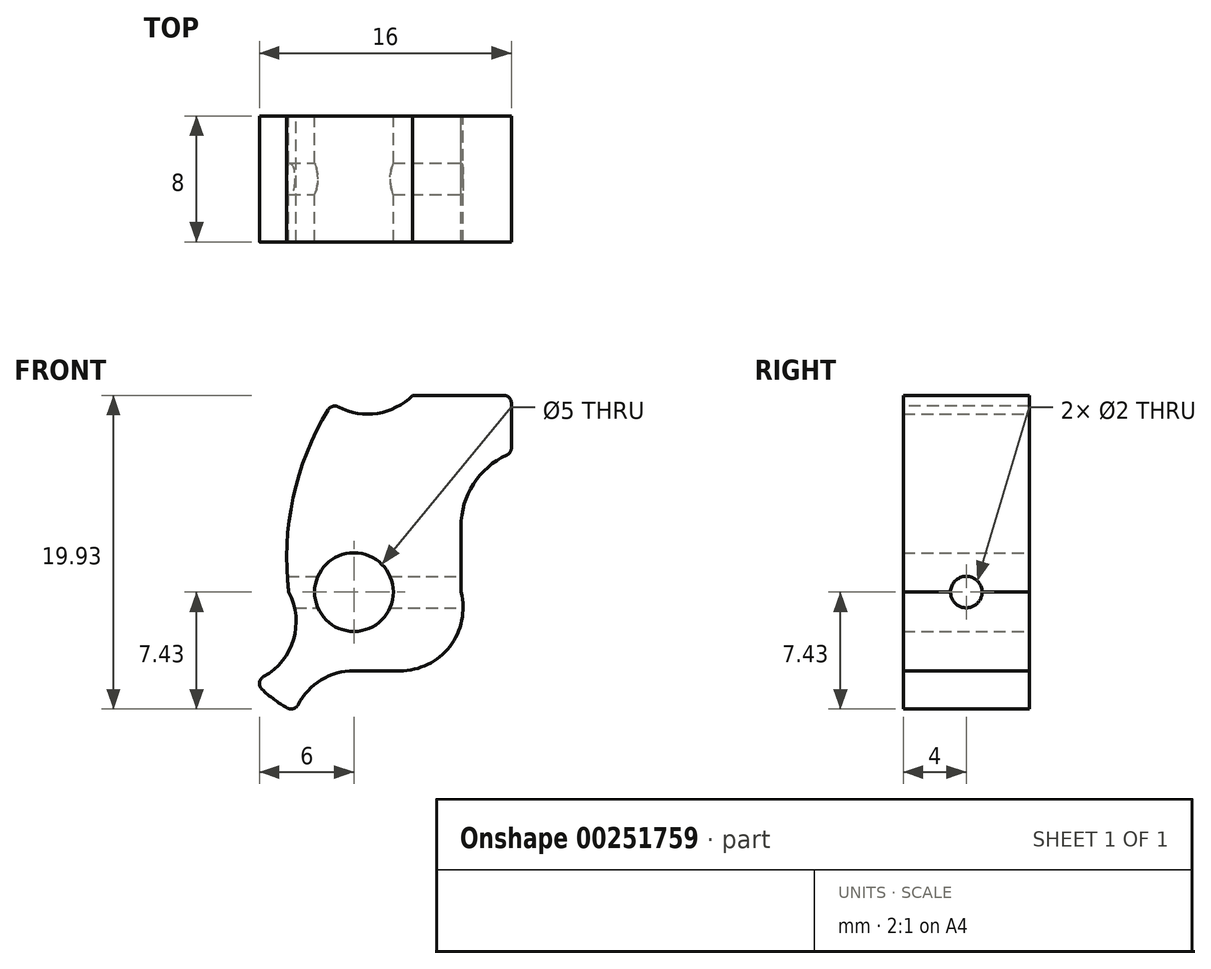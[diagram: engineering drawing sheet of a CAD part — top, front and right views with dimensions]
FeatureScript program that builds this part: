
annotation { "Feature Type Name" : "Feature", "Feature Type Description" : "" }
export const myFeature = defineFeature(function(context is Context, id is Id, definition is map)
    precondition{}
    {
        {
            var Q0;
            Q0=qCreatedBy(makeId("Front.planeOp"),FACE);
            var sketch = newSketch(context, id + "F0", { "sketchPlane" : qUnion([Q0])});
            skCircle(sketch, "E0", {"center": v(0, 0) * mm, "radius": 2.5 * mm});
            skLineSegment(sketch, "E1", {"start": v(0, -5) * mm, "end": v(2.93, -5) * mm});
            skLineSegment(sketch, "E2", {"start": v(6.8, 0) * mm, "end": v(6.8, 4.17) * mm});
            skPoint(sketch, "E3.orphan", {"position": v(6.8, -5) * mm});
            skPoint(sketch, "E4.center.orphan", {"position": v(0, -7) * mm});
            skArc(sketch, "E5", {"start": v(0, -5) * mm, "mid": v(-2.3, -5.72) * mm, "end": v(-3.76, -7.62) * mm});
            skArc(sketch, "E6", {"start": v(-6.36, -5.64) * mm, "mid": v(-5.15, -6.76) * mm, "end": v(-3.76, -7.63) * mm});
            skArc(sketch, "E7", {"start": v(-6.36, -5.64) * mm, "mid": v(-3.95, -3.33) * mm, "end": v(-4.14, 0) * mm});
            skPoint(sketch, "E8.end.orphan", {"position": v(5.8, 0) * mm});
            skArc(sketch, "E9", {"start": v(2.93, -5) * mm, "mid": v(6.09, -3.45) * mm, "end": v(6.8, 0) * mm});
            skLineSegment(sketch, "E10", {"start": v(10, 12.5) * mm, "end": v(10, 8.83) * mm});
            skLineSegment(sketch, "E11", {"start": v(10, 12.5) * mm, "end": v(3.72, 12.5) * mm});
            skArc(sketch, "E12", {"start": v(3.72, 12.5) * mm, "mid": v(1.26, 11.33) * mm, "end": v(-1.38, 12) * mm});
            skArc(sketch, "E13", {"start": v(-1.38, 12) * mm, "mid": v(-3.8, 6.24) * mm, "end": v(-4.14, 0) * mm});
            skArc(sketch, "E14", {"start": v(10, 8.83) * mm, "mid": v(7.68, 7) * mm, "end": v(6.8, 4.17) * mm});
            skSolve(sketch);
        }
        {
            var Q0;
            Q0 = qSketchRegion(id + "F0", true);
            extrude(context, id + "F1", {"entities" : qUnion([Q0]), "depth" : 8 * mm});
        }
        {
            var Q0;
            Q0=makeQuery(id+"F1.opExtrude","SWEPT_EDGE",EDGE,{"disambiguationData":[OSD([sQuery(id+"F0.wireOp",EDGE,"E10"),sQuery(id+"F0.wireOp",EDGE,"E11")])]});
            var Q1;
            Q1=makeQuery(id+"F1.opExtrude","SWEPT_EDGE",EDGE,{"disambiguationData":[OSD([sQuery(id+"F0.wireOp",EDGE,"E12"),sQuery(id+"F0.wireOp",EDGE,"E13")])]});
            var Q2;
            Q2=makeQuery(id+"F1.opExtrude","SWEPT_EDGE",EDGE,{"disambiguationData":[OSD([sQuery(id+"F0.wireOp",EDGE,"E6"),sQuery(id+"F0.wireOp",EDGE,"E7")])]});
            var Q3;
            Q3=makeQuery(id+"F1.opExtrude","SWEPT_EDGE",EDGE,{"disambiguationData":[OSD([sQuery(id+"F0.wireOp",EDGE,"E5"),sQuery(id+"F0.wireOp",EDGE,"E6")])]});
            var Q4;
            Q4=makeQuery(id+"F1.opExtrude","SWEPT_EDGE",EDGE,{"disambiguationData":[OSD([sQuery(id+"F0.wireOp",EDGE,"E10"),sQuery(id+"F0.wireOp",EDGE,"E14")])]});
            fillet(context, id + "F2", {"entities" : qUnion([Q0, Q1, Q2, Q3, Q4]), "radius" : .5 * mm, "tangentPropagation" : true, "allowEdgeOverflow" : false});
        }
        {
            var Q0;
            Q0=makeQuery(id+"F1.opExtrude","SWEPT_FACE",FACE,{"disambiguationData":[OSD([sQuery(id+"F0.wireOp",EDGE,"E2")])]});
            var sketch = newSketch(context, id + "F3", { "sketchPlane" : qUnion([Q0])});
            skCircle(sketch, "E15", {"center": v(-4, 0) * mm, "radius": 1 * mm});
            skSolve(sketch);
        }
        {
            var Q0;
            Q0=makeQuery(id+"F1.opExtrude","SWEPT_FACE",FACE,{"disambiguationData":[OSD([sQuery(id+"F0.wireOp",EDGE,"E10")])]});
            var sketch = newSketch(context, id + "F4", { "sketchPlane" : qUnion([Q0])});
            skCircle(sketch, "E16.0", {"center": v(-4, 0) * mm, "radius": 1 * mm});
            skSolve(sketch);
        }
        {
            var Q0;
            Q0 = qSketchRegion(id + "F4", true);
            extrude(context, id + "F5", {"entities" : qUnion([Q0]), "operationType" : NewBodyOperationType.REMOVE, "endBound" : BoundingType.THROUGH_ALL, "oppositeDirection" : true, "depth" : 25 * mm});
        }
    });
